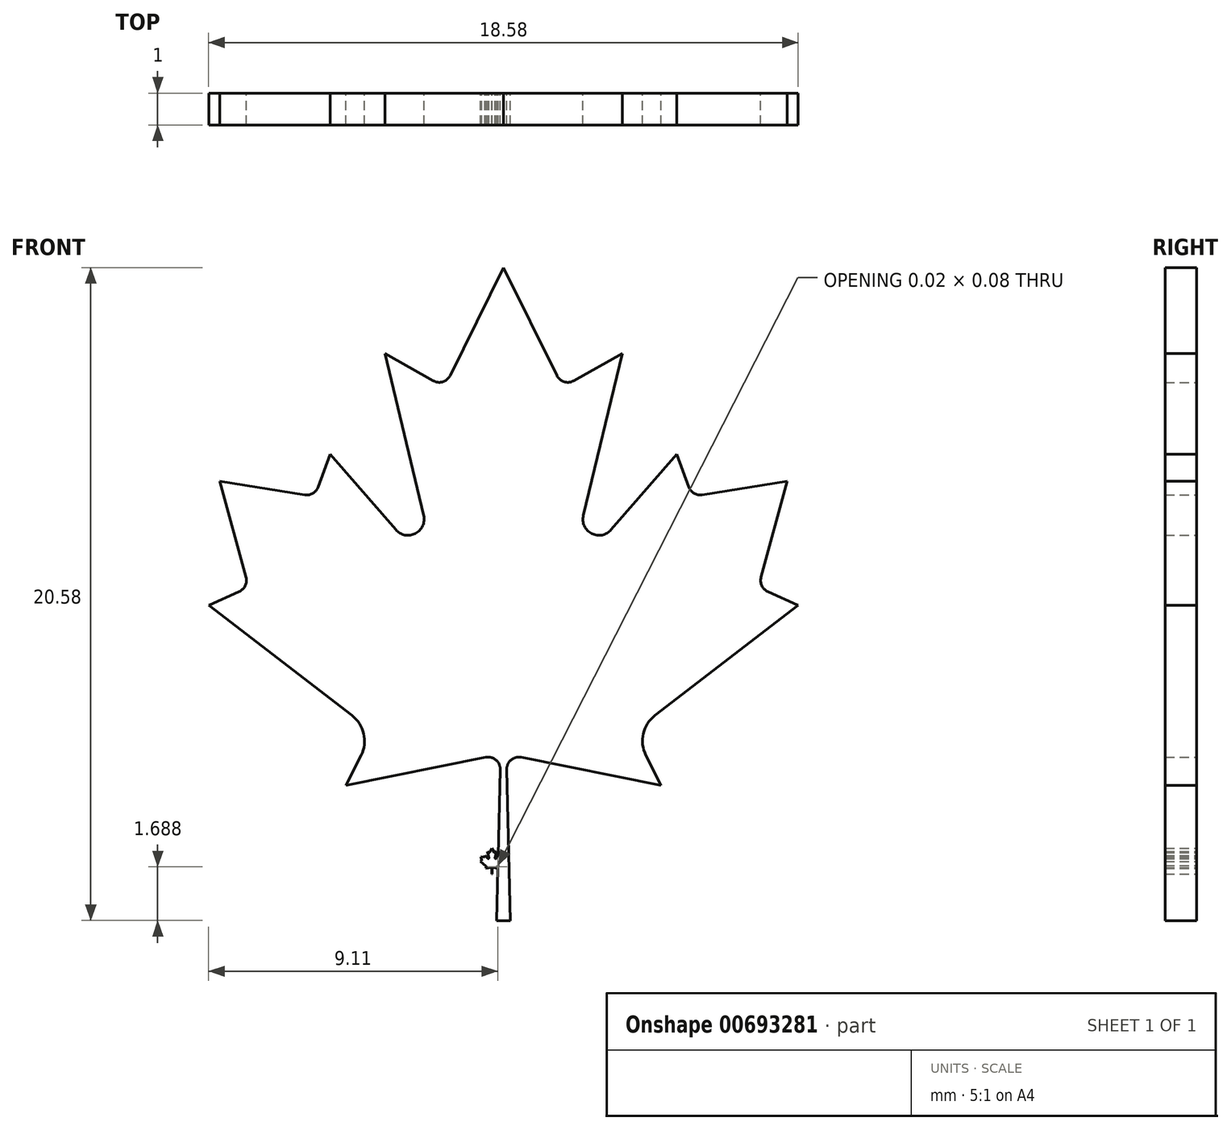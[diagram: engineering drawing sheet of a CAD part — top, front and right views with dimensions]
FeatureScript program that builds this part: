
annotation { "Feature Type Name" : "Feature", "Feature Type Description" : "" }
export const myFeature = defineFeature(function(context is Context, id is Id, definition is map)
    precondition{}
    {
        {
            var Q0;
            Q0=qCreatedBy(makeId("Front.planeOp"),FACE);
            var sketch = newSketch(context, id + "F0", { "sketchPlane" : qUnion([Q0])});
            skLineSegment(sketch, "E0", {"start": v(-0.01, 0.81) * mm, "end": v(-0.01, -0.08) * mm});
            skLineSegment(sketch, "E1", {"start": v(-0.01, 0.81) * mm, "end": v(0.05, 0.68) * mm});
            skLineSegment(sketch, "E2", {"start": v(0.07, 0.67) * mm, "end": v(0.13, 0.7) * mm});
            skLineSegment(sketch, "E3", {"start": v(0.13, 0.7) * mm, "end": v(0.09, 0.5) * mm});
            skLineSegment(sketch, "E4", {"start": v(0.12, 0.49) * mm, "end": v(0.2, 0.58) * mm});
            skLineSegment(sketch, "E5", {"start": v(0.2, 0.58) * mm, "end": v(0.22, 0.54) * mm});
            skLineSegment(sketch, "E6", {"start": v(0.23, 0.53) * mm, "end": v(0.34, 0.55) * mm});
            skLineSegment(sketch, "E7", {"start": v(0.34, 0.55) * mm, "end": v(0.3, 0.43) * mm});
            skLineSegment(sketch, "E8", {"start": v(0.31, 0.4) * mm, "end": v(0.35, 0.4) * mm});
            skLineSegment(sketch, "E9", {"start": v(0.35, 0.4) * mm, "end": v(0.17, 0.26) * mm});
            skLineSegment(sketch, "E10", {"start": v(0.16, 0.2) * mm, "end": v(0.18, 0.17) * mm});
            skLineSegment(sketch, "E11", {"start": v(0.18, 0.17) * mm, "end": v(0, 0.2) * mm});
            skLineSegment(sketch, "E12", {"start": v(0, 0.19) * mm, "end": v(0, 0) * mm});
            skLineSegment(sketch, "E13", {"start": v(0, 0) * mm, "end": v(-0.01, 0) * mm});
            skArc(sketch, "E14", {"start": v(0.05, 0.68) * mm, "mid": v(0.06, 0.67) * mm, "end": v(0.07, 0.67) * mm});
            skArc(sketch, "E15", {"start": v(0.09, 0.5) * mm, "mid": v(0.1, 0.48) * mm, "end": v(0.12, 0.49) * mm});
            skArc(sketch, "E16", {"start": v(0.22, 0.54) * mm, "mid": v(0.22, 0.53) * mm, "end": v(0.23, 0.53) * mm});
            skArc(sketch, "E17", {"start": v(0.3, 0.43) * mm, "mid": v(0.3, 0.42) * mm, "end": v(0.31, 0.4) * mm});
            skArc(sketch, "E18", {"start": v(0.17, 0.26) * mm, "mid": v(0.16, 0.23) * mm, "end": v(0.16, 0.2) * mm});
            skArc(sketch, "E19", {"start": v(0, 0.2) * mm, "mid": v(0, 0.2) * mm, "end": v(0, 0.19) * mm});
            skLineSegment(sketch, "E20", {"start": v(-0.01, 0.81) * mm, "end": v(-0.08, 0.68) * mm});
            skArc(sketch, "E21", {"start": v(-0.1, 0.67) * mm, "mid": v(-0.09, 0.67) * mm, "end": v(-0.08, 0.68) * mm});
            skLineSegment(sketch, "E22", {"start": v(-0.1, 0.67) * mm, "end": v(-0.16, 0.7) * mm});
            skLineSegment(sketch, "E23", {"start": v(-0.16, 0.7) * mm, "end": v(-0.11, 0.5) * mm});
            skLineSegment(sketch, "E24", {"start": v(-0.15, 0.49) * mm, "end": v(-0.23, 0.58) * mm});
            skArc(sketch, "E25", {"start": v(-0.15, 0.49) * mm, "mid": v(-0.12, 0.48) * mm, "end": v(-0.11, 0.5) * mm});
            skLineSegment(sketch, "E26", {"start": v(-0.23, 0.58) * mm, "end": v(-0.24, 0.54) * mm});
            skLineSegment(sketch, "E27", {"start": v(-0.26, 0.53) * mm, "end": v(-0.37, 0.55) * mm});
            skArc(sketch, "E28", {"start": v(-0.26, 0.53) * mm, "mid": v(-0.25, 0.53) * mm, "end": v(-0.24, 0.54) * mm});
            skLineSegment(sketch, "E29", {"start": v(-0.37, 0.55) * mm, "end": v(-0.33, 0.43) * mm});
            skLineSegment(sketch, "E30", {"start": v(-0.34, 0.4) * mm, "end": v(-0.38, 0.4) * mm});
            skArc(sketch, "E31", {"start": v(-0.34, 0.4) * mm, "mid": v(-0.33, 0.42) * mm, "end": v(-0.33, 0.43) * mm});
            skLineSegment(sketch, "E32", {"start": v(-0.38, 0.4) * mm, "end": v(-0.2, 0.26) * mm});
            skArc(sketch, "E33", {"start": v(-0.2, 0.2) * mm, "mid": v(-0.19, 0.23) * mm, "end": v(-0.2, 0.26) * mm});
            skLineSegment(sketch, "E34", {"start": v(-0.2, 0.2) * mm, "end": v(-0.2, 0.17) * mm});
            skLineSegment(sketch, "E35", {"start": v(-0.2, 0.17) * mm, "end": v(-0.04, 0.2) * mm});
            skArc(sketch, "E36", {"start": v(-0.02, 0.19) * mm, "mid": v(-0.02, 0.2) * mm, "end": v(-0.04, 0.2) * mm});
            skLineSegment(sketch, "E37", {"start": v(-0.02, 0.19) * mm, "end": v(-0.02, 0) * mm});
            skLineSegment(sketch, "E38", {"start": v(-0.02, 0) * mm, "end": v(-0.01, 0) * mm});
            skLineSegment(sketch, "E39", {"start": v(0.35, 19.11) * mm, "end": v(0.35, -3.5) * mm});
            skLineSegment(sketch, "E40", {"start": v(0.35, 19.11) * mm, "end": v(2.03, 15.7) * mm});
            skLineSegment(sketch, "E41", {"start": v(2.56, 15.54) * mm, "end": v(4.1, 16.4) * mm});
            skLineSegment(sketch, "E42", {"start": v(4.1, 16.4) * mm, "end": v(2.87, 11.3) * mm});
            skLineSegment(sketch, "E43", {"start": v(3.75, 10.85) * mm, "end": v(5.8, 13.22) * mm});
            skLineSegment(sketch, "E44", {"start": v(5.8, 13.22) * mm, "end": v(6.2, 12.2) * mm});
            skLineSegment(sketch, "E45", {"start": v(6.61, 11.95) * mm, "end": v(9.3, 12.37) * mm});
            skLineSegment(sketch, "E46", {"start": v(9.3, 12.37) * mm, "end": v(8.47, 9.35) * mm});
            skLineSegment(sketch, "E47", {"start": v(8.68, 8.9) * mm, "end": v(9.64, 8.47) * mm});
            skLineSegment(sketch, "E48", {"start": v(9.64, 8.47) * mm, "end": v(5.13, 5) * mm});
            skLineSegment(sketch, "E49", {"start": v(4.84, 3.74) * mm, "end": v(5.32, 2.78) * mm});
            skLineSegment(sketch, "E50", {"start": v(5.32, 2.78) * mm, "end": v(0.91, 3.67) * mm});
            skLineSegment(sketch, "E51", {"start": v(0.46, 3.3) * mm, "end": v(0.56, -1.47) * mm});
            skLineSegment(sketch, "E52", {"start": v(0.56, -1.47) * mm, "end": v(0.35, -1.47) * mm});
            skArc(sketch, "E53", {"start": v(2.03, 15.7) * mm, "mid": v(2.26, 15.51) * mm, "end": v(2.56, 15.54) * mm});
            skArc(sketch, "E54", {"start": v(2.87, 11.3) * mm, "mid": v(3.13, 10.73) * mm, "end": v(3.75, 10.85) * mm});
            skArc(sketch, "E55", {"start": v(6.2, 12.2) * mm, "mid": v(6.36, 12) * mm, "end": v(6.61, 11.95) * mm});
            skArc(sketch, "E56", {"start": v(8.47, 9.35) * mm, "mid": v(8.5, 9.09) * mm, "end": v(8.68, 8.9) * mm});
            skArc(sketch, "E57", {"start": v(5.13, 5) * mm, "mid": v(4.76, 4.42) * mm, "end": v(4.84, 3.74) * mm});
            skArc(sketch, "E58", {"start": v(0.91, 3.67) * mm, "mid": v(0.6, 3.6) * mm, "end": v(0.46, 3.3) * mm});
            skLineSegment(sketch, "E59", {"start": v(0.35, 19.11) * mm, "end": v(-1.33, 15.7) * mm});
            skArc(sketch, "E60", {"start": v(-1.86, 15.54) * mm, "mid": v(-1.56, 15.51) * mm, "end": v(-1.33, 15.7) * mm});
            skLineSegment(sketch, "E61", {"start": v(-1.86, 15.54) * mm, "end": v(-3.39, 16.4) * mm});
            skLineSegment(sketch, "E62", {"start": v(-3.39, 16.4) * mm, "end": v(-2.16, 11.3) * mm});
            skLineSegment(sketch, "E63", {"start": v(-3.04, 10.85) * mm, "end": v(-5.1, 13.22) * mm});
            skArc(sketch, "E64", {"start": v(-3.04, 10.85) * mm, "mid": v(-2.43, 10.73) * mm, "end": v(-2.16, 11.3) * mm});
            skLineSegment(sketch, "E65", {"start": v(-5.1, 13.22) * mm, "end": v(-5.5, 12.2) * mm});
            skLineSegment(sketch, "E66", {"start": v(-5.9, 11.95) * mm, "end": v(-8.6, 12.37) * mm});
            skArc(sketch, "E67", {"start": v(-5.9, 11.95) * mm, "mid": v(-5.66, 12) * mm, "end": v(-5.5, 12.2) * mm});
            skLineSegment(sketch, "E68", {"start": v(-8.6, 12.37) * mm, "end": v(-7.76, 9.35) * mm});
            skLineSegment(sketch, "E69", {"start": v(-7.98, 8.9) * mm, "end": v(-8.94, 8.47) * mm});
            skArc(sketch, "E70", {"start": v(-7.98, 8.9) * mm, "mid": v(-7.79, 9.09) * mm, "end": v(-7.76, 9.35) * mm});
            skLineSegment(sketch, "E71", {"start": v(-8.94, 8.47) * mm, "end": v(-4.42, 5) * mm});
            skArc(sketch, "E72", {"start": v(-4.14, 3.74) * mm, "mid": v(-4.05, 4.42) * mm, "end": v(-4.42, 5) * mm});
            skLineSegment(sketch, "E73", {"start": v(-4.14, 3.74) * mm, "end": v(-4.61, 2.78) * mm});
            skLineSegment(sketch, "E74", {"start": v(-4.61, 2.78) * mm, "end": v(-0.2, 3.67) * mm});
            skArc(sketch, "E75", {"start": v(0.25, 3.3) * mm, "mid": v(0.11, 3.6) * mm, "end": v(-0.2, 3.67) * mm});
            skLineSegment(sketch, "E76", {"start": v(0.25, 3.3) * mm, "end": v(0.14, -1.47) * mm});
            skLineSegment(sketch, "E77", {"start": v(0.14, -1.47) * mm, "end": v(0.35, -1.47) * mm});
            skSolve(sketch);
        }
        {
            var Q0;
            Q0 = qSketchRegion(id + "F0", true);
            extrude(context, id + "F1", {"entities" : qUnion([Q0]), "depth" : 1 * mm, "offsetDistance" : 25 * mm});
        }
    });
